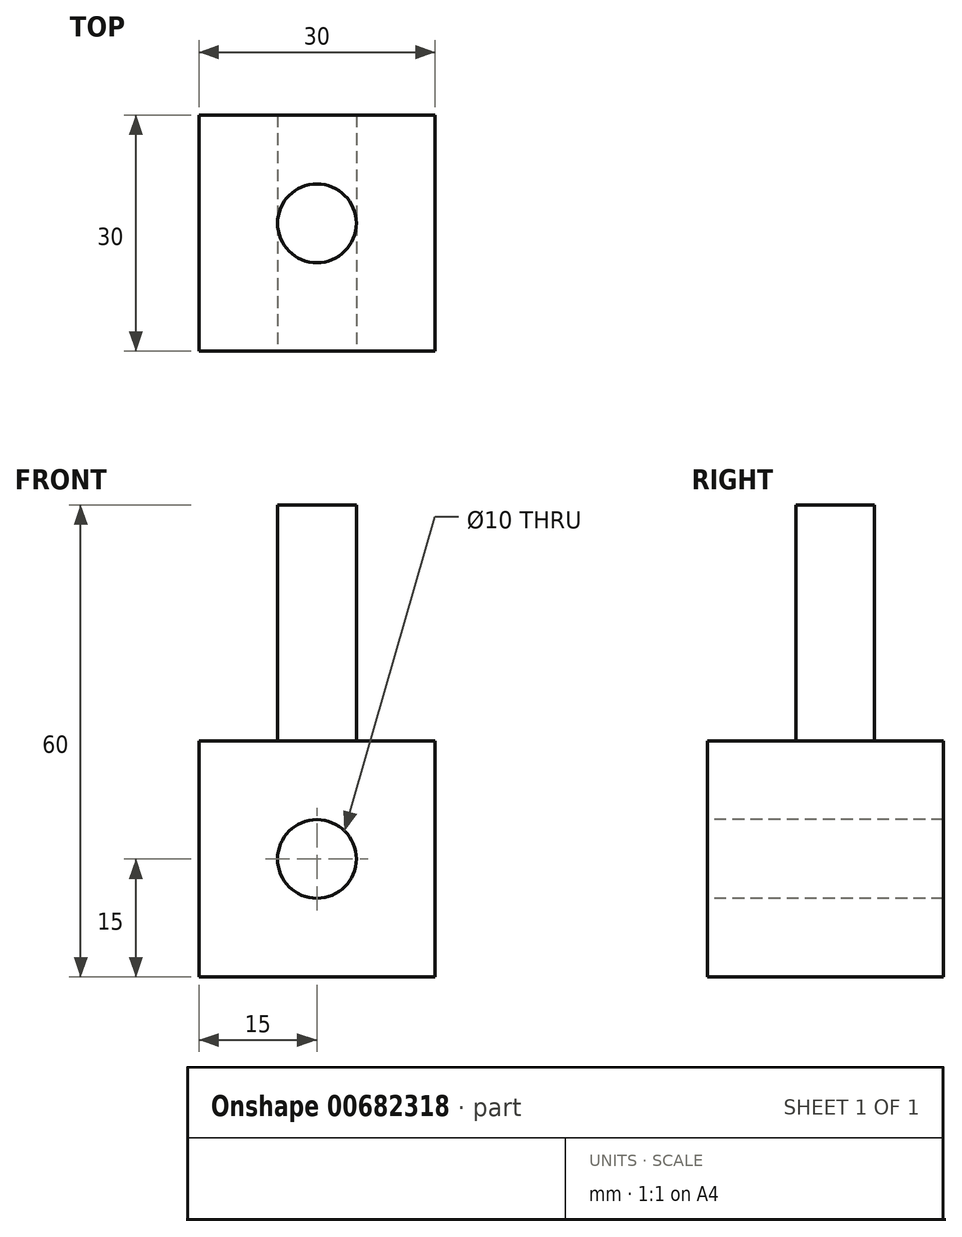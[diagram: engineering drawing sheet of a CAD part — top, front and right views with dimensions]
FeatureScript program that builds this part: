
annotation { "Feature Type Name" : "Feature", "Feature Type Description" : "" }
export const myFeature = defineFeature(function(context is Context, id is Id, definition is map)
    precondition{}
    {
        {
            var Q0;
            Q0=qCreatedBy(makeId("Front.planeOp"),FACE);
            var sketch = newSketch(context, id + "F0", { "sketchPlane" : qUnion([Q0])});
            skLineSegment(sketch, "E0.bottom", {"start": v(15, 15) * mm, "end": v(-15, 15) * mm});
            skLineSegment(sketch, "E0.top", {"start": v(15, -15) * mm, "end": v(-15, -15) * mm});
            skLineSegment(sketch, "E0.left", {"start": v(15, 15) * mm, "end": v(15, -15) * mm});
            skLineSegment(sketch, "E0.right", {"start": v(-15, 15) * mm, "end": v(-15, -15) * mm});
            skPoint(sketch, "E0.middle", {"position": v(0, 0) * mm});
            skSolve(sketch);
        }
        {
            var Q0;
            Q0 = qSketchRegion(id + "F0", true);
            extrude(context, id + "F1", {"entities" : qUnion([Q0]), "depth" : 30 * mm, "offsetDistance" : 25 * mm});
        }
        {
            var Q0;
            Q0=makeQuery(id+"F1.opExtrude","CAP_FACE",FACE,{"disambiguationData":[OSD([sQuery(id+"F0.wireOp",EDGE,"E0.bottom"),sQuery(id+"F0.wireOp",EDGE,"E0.top"),sQuery(id+"F0.wireOp",EDGE,"E0.left"),sQuery(id+"F0.wireOp",EDGE,"E0.right")])],"isStart":false});
            var sketch = newSketch(context, id + "F2", { "sketchPlane" : qUnion([Q0])});
            skSolve(sketch);
        }
        {
            var Q0;
            Q0=makeQuery(id+"F2.imprint","IMPRINT",FACE,{"disambiguationData":[TD([[makeQuery(id+"F2.imprint","IMPRINT",EDGE,{"derivedFrom":makeQuery(id+"F1.opExtrude","CAP_EDGE",EDGE,{"disambiguationData":[OSD([sQuery(id+"F0.wireOp",EDGE,"E0.bottom")])],"isStart":false})}),1.0]])]});
            var sketch = newSketch(context, id + "F3", { "sketchPlane" : qUnion([Q0])});
            skCircle(sketch, "E1", {"center": v(0, 0) * mm, "radius": 5 * mm});
            skSolve(sketch);
        }
        {
            var Q0;
            Q0 = qSketchRegion(id + "F3", true);
            extrude(context, id + "F4", {"entities" : qUnion([Q0]), "operationType" : NewBodyOperationType.REMOVE, "oppositeDirection" : true, "depth" : 30.2 * mm, "offsetDistance" : 25 * mm});
        }
        {
            var Q0;
            Q0=makeQuery(id+"F1.opExtrude","SWEPT_FACE",FACE,{"disambiguationData":[OSD([sQuery(id+"F0.wireOp",EDGE,"E0.bottom")])]});
            var sketch = newSketch(context, id + "F5", { "sketchPlane" : qUnion([Q0])});
            skCircle(sketch, "E2", {"center": v(0, -13.74) * mm, "radius": 5 * mm});
            skSolve(sketch);
        }
        {
            var Q0;
            Q0=makeQuery(id+"F5.imprint","IMPRINT",FACE,{"disambiguationData":[TD([[makeQuery(id+"F5.imprint","IMPRINT",EDGE,{"derivedFrom":sQuery(id+"F5.wireOp",EDGE,"E2")}),1.0]])]});
            var Q1;
            Q1=sQuery(id+"F5.wireOp",EDGE,"E2");
            extrude(context, id + "F6", {"entities" : qUnion([Q0]), "operationType" : NewBodyOperationType.ADD, "surfaceEntities" : qUnion([Q1]), "depth" : 30 * mm, "offsetDistance" : 25 * mm});
        }
    });
